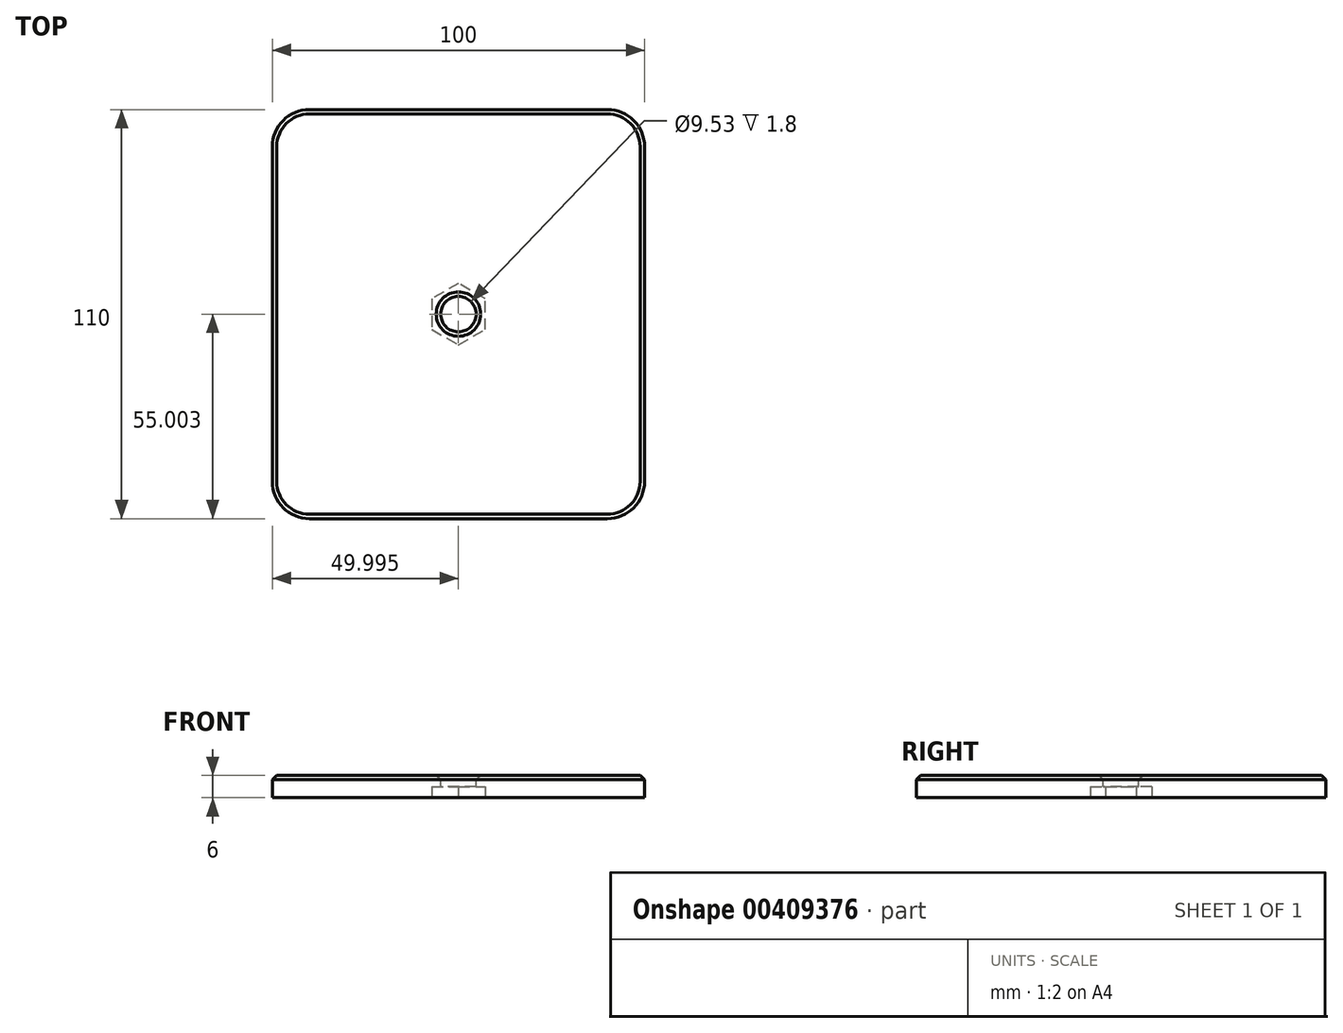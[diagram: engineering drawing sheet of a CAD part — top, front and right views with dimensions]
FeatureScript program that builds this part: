
annotation { "Feature Type Name" : "Feature", "Feature Type Description" : "" }
export const myFeature = defineFeature(function(context is Context, id is Id, definition is map)
    precondition{}
    {
        {
            var Q0;
            Q0=qCreatedBy(makeId("Top.planeOp"),FACE);
            var sketch = newSketch(context, id + "F0", { "sketchPlane" : qUnion([Q0])});
            skLineSegment(sketch, "E0.bottom", {"start": v(-20.21, -57.17) * mm, "end": v(59.79, -57.17) * mm});
            skLineSegment(sketch, "E0.top", {"start": v(-20.21, 52.83) * mm, "end": v(59.79, 52.83) * mm});
            skLineSegment(sketch, "E0.left", {"start": v(-30.21, -47.17) * mm, "end": v(-30.21, 42.83) * mm});
            skLineSegment(sketch, "E0.right", {"start": v(69.79, -47.17) * mm, "end": v(69.79, 42.83) * mm});
            skPoint(sketch, "E1.visualSharp", {"position": v(-30.21, 52.83) * mm});
            skArc(sketch, "E1.filletArc", {"start": v(-20.21, 52.83) * mm, "mid": v(-27.29, 49.9) * mm, "end": v(-30.21, 42.83) * mm});
            skPoint(sketch, "E2.visualSharp", {"position": v(69.79, 52.83) * mm});
            skArc(sketch, "E2.filletArc", {"start": v(69.79, 42.83) * mm, "mid": v(66.86, 49.9) * mm, "end": v(59.79, 52.83) * mm});
            skPoint(sketch, "E3.visualSharp", {"position": v(69.79, -57.17) * mm});
            skArc(sketch, "E3.filletArc", {"start": v(59.79, -57.17) * mm, "mid": v(66.86, -54.24) * mm, "end": v(69.79, -47.17) * mm});
            skPoint(sketch, "E4.visualSharp", {"position": v(-30.21, -57.17) * mm});
            skArc(sketch, "E4.filletArc", {"start": v(-30.21, -47.17) * mm, "mid": v(-27.29, -54.24) * mm, "end": v(-20.21, -57.17) * mm});
            skSolve(sketch);
        }
        {
            var Q0;
            Q0=makeQuery(id+"F0.imprint","IMPRINT",FACE,{"disambiguationData":[TD([[makeQuery(id+"F0.imprint","IMPRINT",EDGE,{"derivedFrom":sQuery(id+"F0.wireOp",EDGE,"E0.bottom")}),1.0]])]});
            extrude(context, id + "F1", {"entities" : qUnion([Q0]), "depth" : 6 * mm});
        }
        {
            var Q0;
            Q0=makeQuery(id+"F1.opExtrude","CAP_FACE",FACE,{"disambiguationData":[OSD([sQuery(id+"F0.wireOp",EDGE,"E0.bottom"),sQuery(id+"F0.wireOp",EDGE,"E0.top"),sQuery(id+"F0.wireOp",EDGE,"E0.left"),sQuery(id+"F0.wireOp",EDGE,"E0.right")])],"isStart":false});
            var sketch = newSketch(context, id + "F2", { "sketchPlane" : qUnion([Q0])});
            skCircle(sketch, "E5", {"center": v(19.79, -2.17) * mm, "radius": 4.76 * mm});
            skSolve(sketch);
        }
        {
            var Q0;
            Q0=makeQuery(id+"F2.imprint","IMPRINT",FACE,{"disambiguationData":[TD([[makeQuery(id+"F2.imprint","IMPRINT",EDGE,{"derivedFrom":sQuery(id+"F2.wireOp",EDGE,"E5")}),1.0]])]});
            extrude(context, id + "F3", {"entities" : qUnion([Q0]), "operationType" : NewBodyOperationType.REMOVE, "oppositeDirection" : true, "depth" : 25 * mm});
        }
        {
            var Q0;
            Q0=makeQuery(id+"F1.opExtrude","CAP_FACE",FACE,{"disambiguationData":[OSD([sQuery(id+"F0.wireOp",EDGE,"E0.bottom"),sQuery(id+"F0.wireOp",EDGE,"E0.top"),sQuery(id+"F0.wireOp",EDGE,"E0.left"),sQuery(id+"F0.wireOp",EDGE,"E0.right")])],"isStart":true});
            var sketch = newSketch(context, id + "F4", { "sketchPlane" : qUnion([Q0])});
            skCircle(sketch, "E6.cCircle", {"center": v(19.79, 2.17) * mm, "radius": 7.15 * mm, "construction": true});
            skLineSegment(sketch, "E6.0", {"start": v(26.94, 6.3) * mm, "end": v(26.94, -1.96) * mm});
            skLineSegment(sketch, "E6.1", {"start": v(26.94, -1.96) * mm, "end": v(19.79, -6.09) * mm});
            skLineSegment(sketch, "E6.2", {"start": v(19.79, -6.09) * mm, "end": v(12.64, -1.96) * mm});
            skLineSegment(sketch, "E6.3", {"start": v(12.64, -1.96) * mm, "end": v(12.64, 6.3) * mm});
            skLineSegment(sketch, "E6.4", {"start": v(12.64, 6.3) * mm, "end": v(19.79, 10.42) * mm});
            skLineSegment(sketch, "E6.5", {"start": v(19.79, 10.42) * mm, "end": v(26.94, 6.3) * mm});
            skPoint(sketch, "E6.0.midPoint", {"position": v(26.94, 2.17) * mm});
            skSolve(sketch);
        }
        {
            var Q0;
            Q0=makeQuery(id+"F4.imprint","IMPRINT",FACE,{"disambiguationData":[TD([[makeQuery(id+"F4.imprint","IMPRINT",EDGE,{"derivedFrom":sQuery(id+"F4.wireOp",EDGE,"E6.0")}),-1.0]])]});
            extrude(context, id + "F5", {"entities" : qUnion([Q0]), "operationType" : NewBodyOperationType.REMOVE, "oppositeDirection" : true, "depth" : 3 * mm});
        }
        {
            var Q0;
            Q0=makeQuery(id+"F1.opExtrude","CAP_FACE",FACE,{"disambiguationData":[OSD([sQuery(id+"F0.wireOp",EDGE,"E0.bottom"),sQuery(id+"F0.wireOp",EDGE,"E0.top"),sQuery(id+"F0.wireOp",EDGE,"E0.left"),sQuery(id+"F0.wireOp",EDGE,"E0.right"),sQuery(id+"F0.wireOp",EDGE,"E1.filletArc"),sQuery(id+"F0.wireOp",EDGE,"E2.filletArc"),sQuery(id+"F0.wireOp",EDGE,"E3.filletArc"),sQuery(id+"F0.wireOp",EDGE,"E4.filletArc")])],"isStart":false});
            chamfer(context, id + "F6", {"entities" : qUnion([Q0]), "width" : 1.2 * mm, "tangentPropagation" : true});
        }
    });
